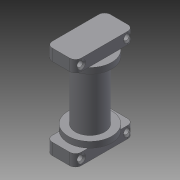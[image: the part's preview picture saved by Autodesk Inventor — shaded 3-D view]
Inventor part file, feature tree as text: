
AUTODESK INVENTOR PART (.ipt)
format: ipt  version: 2015 (Build 190159000, 159)  size: 196,608 bytes
history: native  units: mm
features: sketch x8, extrude x6, hole x2, fillet x1
ambient origin geometry x8: Origin, YZ Plane, XZ Plane, XY Plane, X Axis, Y Axis, Z Axis, Center Point
bodies: Solid1 (feature_tree)
feature tree (17):
  extrude  "Extrusion1"  Depth=10.0mm
  extrude  "Extrusion2"  Depth=15.0mm
  extrude  "Extrusion3"  Depth=2.0mm TaperAngle=0.0deg
  extrude  "Extrusion4"  Depth=10.0mm
  extrude  "Extrusion5"  Depth=7.5mm
  hole  "Hole1"  [1 undecoded]
  extrude  "Extrusion6"  Depth=4.0mm TaperAngle=0.0deg
  hole  "Hole2"  [1 undecoded]
  fillet  "Fillet1"  Radius=2.0mm
  sketch  "Sketch1"  dims[d0=5.5mm d1=10.0mm]
  sketch  "Sketch2"  dims[d2=20.0mm d3=0.0mm d4=15.0mm]
  sketch  "Sketch3"  dims[d5=2.0mm d6=0.0mm d7=2.0mm d8=0.0mm]
  sketch  "Sketch4"  dims[d9=10.0mm d10=10.0mm]
  sketch  "Sketch5"  dims[d11=7.5mm d12=7.5mm]
  sketch  "Sketch6"  dims[d13=4.0mm d14=0.0mm d15=10.0mm]
  sketch  "Sketch7"  dims[d16=2.5mm d17=4.0mm d18=0.0mm]
  sketch  "Sketch8"  dims[d19=2.0mm d20=2.0mm d21=2.0mm d22=2.0mm d23=2.0mm d24=6.0mm d25=3.0mm d26=2.0mm d27=90.0deg d28=10.0mm d29=20.594885mm d30=4.0mm d31=0.0mm d32=2.0mm d33=2.0mm d34=2.0mm d35=6.0mm d36=3.0mm d37=2.0mm d38=90.0deg d39=10.0mm d40=20.594885mm d41=2.0mm]
note: 2 required parameter values undecoded (feature->parameter linkage not recoverable at this tier; creation-order binding heuristic only, values carry confidence <= 0.55)
